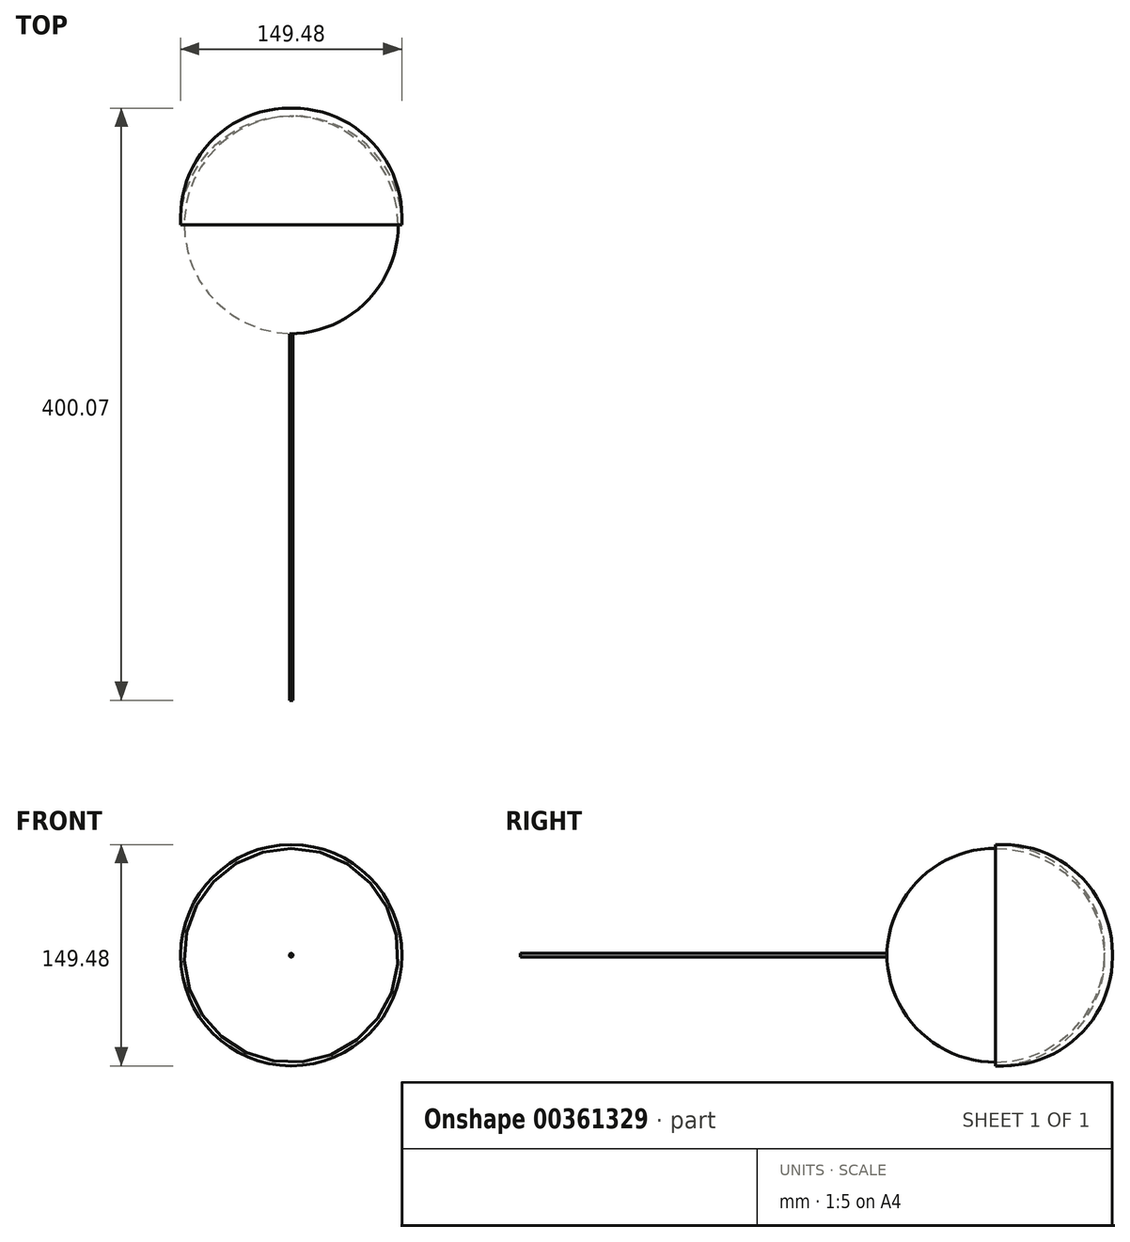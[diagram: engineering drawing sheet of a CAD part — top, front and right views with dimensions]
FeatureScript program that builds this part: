
annotation { "Feature Type Name" : "Feature", "Feature Type Description" : "" }
export const myFeature = defineFeature(function(context is Context, id is Id, definition is map)
    precondition{}
    {
        {
            var Q0;
            Q0=qCreatedBy(makeId("Front.planeOp"),FACE);
            var sketch = newSketch(context, id + "F0", { "sketchPlane" : qUnion([Q0])});
            skCircle(sketch, "E0", {"center": v(0, 0) * mm, "radius": 74.74 * mm});
            skSolve(sketch);
        }
        {
            var Q0;
            Q0 = qSketchRegion(id + "F0", true);
            extrude(context, id + "F1", {"entities" : qUnion([Q0]), "endBound" : BoundingType.SYMMETRIC, "depth" : 152.4 * mm});
        }
        {
            var Q0;
            Q0=makeQuery(id+"F1.opExtrude","SWEPT_FACE",FACE,{"disambiguationData":[OSD([sQuery(id+"F0.wireOp",EDGE,"E0")])]});
            fillet(context, id + "F2", {"entities" : qUnion([Q0]), "radius" : 73.52 * mm, "tangentPropagation" : true, "allowEdgeOverflow" : false});
        }
        {
            var Q0;
            Q0=makeQuery(id+"F1.opExtrude","CAP_FACE",FACE,{"disambiguationData":[OSD([sQuery(id+"F0.wireOp",EDGE,"E0")])],"isStart":false});
            extrude(context, id + "F3", {"entities" : qUnion([Q0]), "operationType" : NewBodyOperationType.ADD, "depth" : 247.67 * mm});
        }
    });
